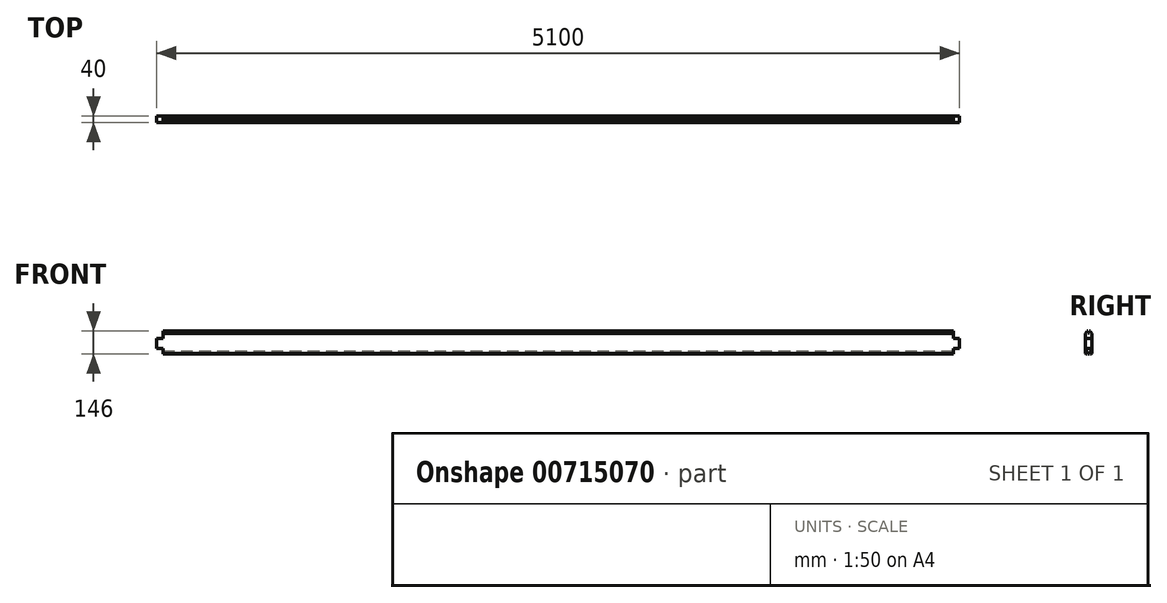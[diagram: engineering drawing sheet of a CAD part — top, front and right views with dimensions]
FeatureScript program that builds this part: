
annotation { "Feature Type Name" : "Feature", "Feature Type Description" : "" }
export const myFeature = defineFeature(function(context is Context, id is Id, definition is map)
    precondition{}
    {
        {
            var Q0;
            Q0=qCreatedBy(makeId("Right.planeOp"),FACE);
            var sketch = newSketch(context, id + "F0", { "sketchPlane" : qUnion([Q0])});
            skLineSegment(sketch, "E0", {"start": v(20, 56) * mm, "end": v(20, -70) * mm});
            skLineSegment(sketch, "E1", {"start": v(20, -70) * mm, "end": v(17, -73) * mm});
            skLineSegment(sketch, "E2", {"start": v(17, -73) * mm, "end": v(12, -73) * mm});
            skLineSegment(sketch, "E3", {"start": v(12, -59) * mm, "end": v(12, -73) * mm});
            skLineSegment(sketch, "E4", {"start": v(12, -59) * mm, "end": v(4, -59) * mm});
            skLineSegment(sketch, "E5", {"start": v(4, -73) * mm, "end": v(4, -59) * mm});
            skLineSegment(sketch, "E6", {"start": v(4, -73) * mm, "end": v(-4, -73) * mm});
            skLineSegment(sketch, "E7", {"start": v(-4, -59) * mm, "end": v(-4, -73) * mm});
            skLineSegment(sketch, "E8", {"start": v(-4, -59) * mm, "end": v(-12, -59) * mm});
            skLineSegment(sketch, "E9", {"start": v(-12, -73) * mm, "end": v(-12, -59) * mm});
            skLineSegment(sketch, "E10", {"start": v(-12, -73) * mm, "end": v(-17, -73) * mm});
            skLineSegment(sketch, "E11", {"start": v(-17, -73) * mm, "end": v(-20, -70) * mm});
            skLineSegment(sketch, "E12", {"start": v(-20, -70) * mm, "end": v(-20, 56) * mm});
            skLineSegment(sketch, "E13", {"start": v(-20, 56) * mm, "end": v(-17, 59) * mm});
            skLineSegment(sketch, "E14", {"start": v(-17, 59) * mm, "end": v(-12, 59) * mm});
            skLineSegment(sketch, "E15", {"start": v(-4, 59) * mm, "end": v(4, 59) * mm});
            skLineSegment(sketch, "E16", {"start": v(12, 59) * mm, "end": v(17, 59) * mm});
            skLineSegment(sketch, "E17", {"start": v(17, 59) * mm, "end": v(20, 56) * mm});
            skPoint(sketch, "E18.end.orphan", {"position": v(12, 57.8) * mm});
            skPoint(sketch, "E19.end.orphan", {"position": v(4, 66.3) * mm});
            skPoint(sketch, "E20.end.orphan", {"position": v(-4, 66.3) * mm});
            skLineSegment(sketch, "E21", {"start": v(-12, 59) * mm, "end": v(-12, 73) * mm});
            skLineSegment(sketch, "E22", {"start": v(-12, 73) * mm, "end": v(-4, 73) * mm});
            skLineSegment(sketch, "E23", {"start": v(-4, 73) * mm, "end": v(-4, 59) * mm});
            skLineSegment(sketch, "E24", {"start": v(4, 59) * mm, "end": v(4, 73) * mm});
            skLineSegment(sketch, "E25", {"start": v(4, 73) * mm, "end": v(12, 73) * mm});
            skLineSegment(sketch, "E26", {"start": v(12, 73) * mm, "end": v(12, 59) * mm});
            skSolve(sketch);
        }
        {
            var Q0;
            Q0=makeQuery(id+"F0.imprint","IMPRINT",FACE,{"disambiguationData":[TD([[makeQuery(id+"F0.imprint","IMPRINT",EDGE,{"derivedFrom":sQuery(id+"F0.wireOp",EDGE,"E0")}),-1.0]])]});
            extrude(context, id + "F1", {"entities" : qUnion([Q0]), "endBound" : BoundingType.SYMMETRIC, "depth" : 5100 * mm, "offsetDistance" : 25 * mm});
        }
        {
            var Q0;
            Q0=qCreatedBy(makeId("Front.planeOp"),FACE);
            var sketch = newSketch(context, id + "F2", { "sketchPlane" : qUnion([Q0])});
            skLineSegment(sketch, "E27.bottom", {"start": v(-2510, 92) * mm, "end": v(-2590, 92) * mm});
            skLineSegment(sketch, "E27.top", {"start": v(-2510, 26) * mm, "end": v(-2590, 26) * mm});
            skLineSegment(sketch, "E27.left", {"start": v(-2510, 92) * mm, "end": v(-2510, 26) * mm});
            skLineSegment(sketch, "E27.right", {"start": v(-2590, 92) * mm, "end": v(-2590, 26) * mm});
            skPoint(sketch, "E27.middle", {"position": v(-2550, 59) * mm});
            skLineSegment(sketch, "E28.bottom", {"start": v(-2510, -40) * mm, "end": v(-2590, -40) * mm});
            skLineSegment(sketch, "E28.top", {"start": v(-2510, -106) * mm, "end": v(-2590, -106) * mm});
            skLineSegment(sketch, "E28.left", {"start": v(-2510, -40) * mm, "end": v(-2510, -106) * mm});
            skLineSegment(sketch, "E28.right", {"start": v(-2590, -40) * mm, "end": v(-2590, -106) * mm});
            skPoint(sketch, "E28.middle", {"position": v(-2550, -73) * mm});
            skLineSegment(sketch, "E29.bottom", {"start": v(2510, 92) * mm, "end": v(2590, 92) * mm});
            skLineSegment(sketch, "E29.top", {"start": v(2510, 26) * mm, "end": v(2590, 26) * mm});
            skLineSegment(sketch, "E29.left", {"start": v(2510, 92) * mm, "end": v(2510, 26) * mm});
            skLineSegment(sketch, "E29.right", {"start": v(2590, 92) * mm, "end": v(2590, 26) * mm});
            skPoint(sketch, "E29.middle", {"position": v(2550, 59) * mm});
            skLineSegment(sketch, "E30.bottom", {"start": v(2510, -106) * mm, "end": v(2590, -106) * mm});
            skLineSegment(sketch, "E30.top", {"start": v(2510, -40) * mm, "end": v(2590, -40) * mm});
            skLineSegment(sketch, "E30.left", {"start": v(2510, -106) * mm, "end": v(2510, -40) * mm});
            skLineSegment(sketch, "E30.right", {"start": v(2590, -106) * mm, "end": v(2590, -40) * mm});
            skPoint(sketch, "E30.middle", {"position": v(2550, -73) * mm});
            skSolve(sketch);
        }
        {
            var Q0;
            Q0=makeQuery(id+"F2.imprint","IMPRINT",FACE,{"disambiguationData":[TD([[makeQuery(id+"F2.imprint","IMPRINT",EDGE,{"derivedFrom":sQuery(id+"F2.wireOp",EDGE,"E27.bottom")}),1.0]])]});
            var Q1;
            Q1=makeQuery(id+"F2.imprint","IMPRINT",FACE,{"disambiguationData":[TD([[makeQuery(id+"F2.imprint","IMPRINT",EDGE,{"derivedFrom":sQuery(id+"F2.wireOp",EDGE,"E28.bottom")}),1.0]])]});
            var Q2;
            Q2=makeQuery(id+"F2.imprint","IMPRINT",FACE,{"disambiguationData":[TD([[makeQuery(id+"F2.imprint","IMPRINT",EDGE,{"derivedFrom":sQuery(id+"F2.wireOp",EDGE,"E29.bottom")}),-1.0]])]});
            var Q3;
            Q3=makeQuery(id+"F2.imprint","IMPRINT",FACE,{"disambiguationData":[TD([[makeQuery(id+"F2.imprint","IMPRINT",EDGE,{"derivedFrom":sQuery(id+"F2.wireOp",EDGE,"E30.bottom")}),1.0]])]});
            extrude(context, id + "F3", {"entities" : qUnion([Q0, Q1, Q2, Q3]), "operationType" : NewBodyOperationType.REMOVE, "endBound" : BoundingType.SYMMETRIC, "oppositeDirection" : true, "depth" : 100 * mm, "offsetDistance" : 25 * mm});
        }
    });
